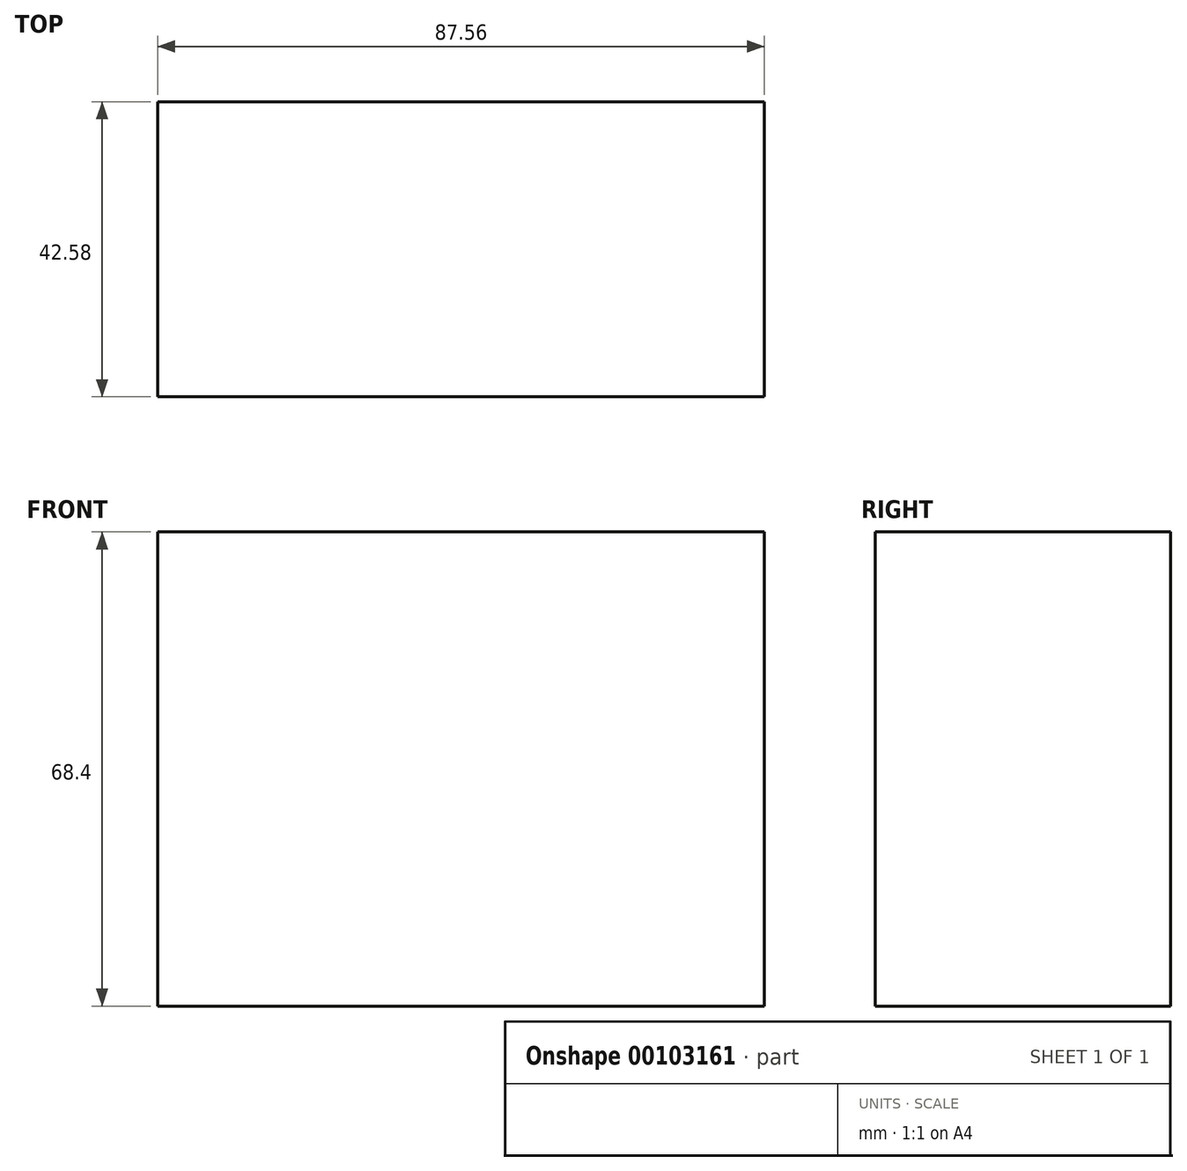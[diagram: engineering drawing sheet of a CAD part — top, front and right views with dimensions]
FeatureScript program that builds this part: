
annotation { "Feature Type Name" : "Feature", "Feature Type Description" : "" }
export const myFeature = defineFeature(function(context is Context, id is Id, definition is map)
    precondition{}
    {
        {
            var Q0;
            Q0=qCreatedBy(makeId("Front.planeOp"),FACE);
            var sketch = newSketch(context, id + "F0", { "sketchPlane" : qUnion([Q0])});
            skLineSegment(sketch, "E0.bottom", {"start": v(43.78, 34.2) * mm, "end": v(-43.78, 34.2) * mm});
            skLineSegment(sketch, "E0.top", {"start": v(43.78, -34.2) * mm, "end": v(-43.78, -34.2) * mm});
            skLineSegment(sketch, "E0.left", {"start": v(43.78, 34.2) * mm, "end": v(43.78, -34.2) * mm});
            skLineSegment(sketch, "E0.right", {"start": v(-43.78, 34.2) * mm, "end": v(-43.78, -34.2) * mm});
            skPoint(sketch, "E0.middle", {"position": v(0, 0) * mm});
            skSolve(sketch);
        }
        {
            var Q0;
            Q0=makeQuery(id+"F0.imprint","IMPRINT",FACE,{"disambiguationData":[TD([[makeQuery(id+"F0.imprint","IMPRINT",EDGE,{"derivedFrom":sQuery(id+"F0.wireOp",EDGE,"E0.bottom")}),1.0]])]});
            extrude(context, id + "F1", {"entities" : qUnion([Q0]), "endBound" : BoundingType.SYMMETRIC, "depth" : 42.6 * mm});
        }
    });
